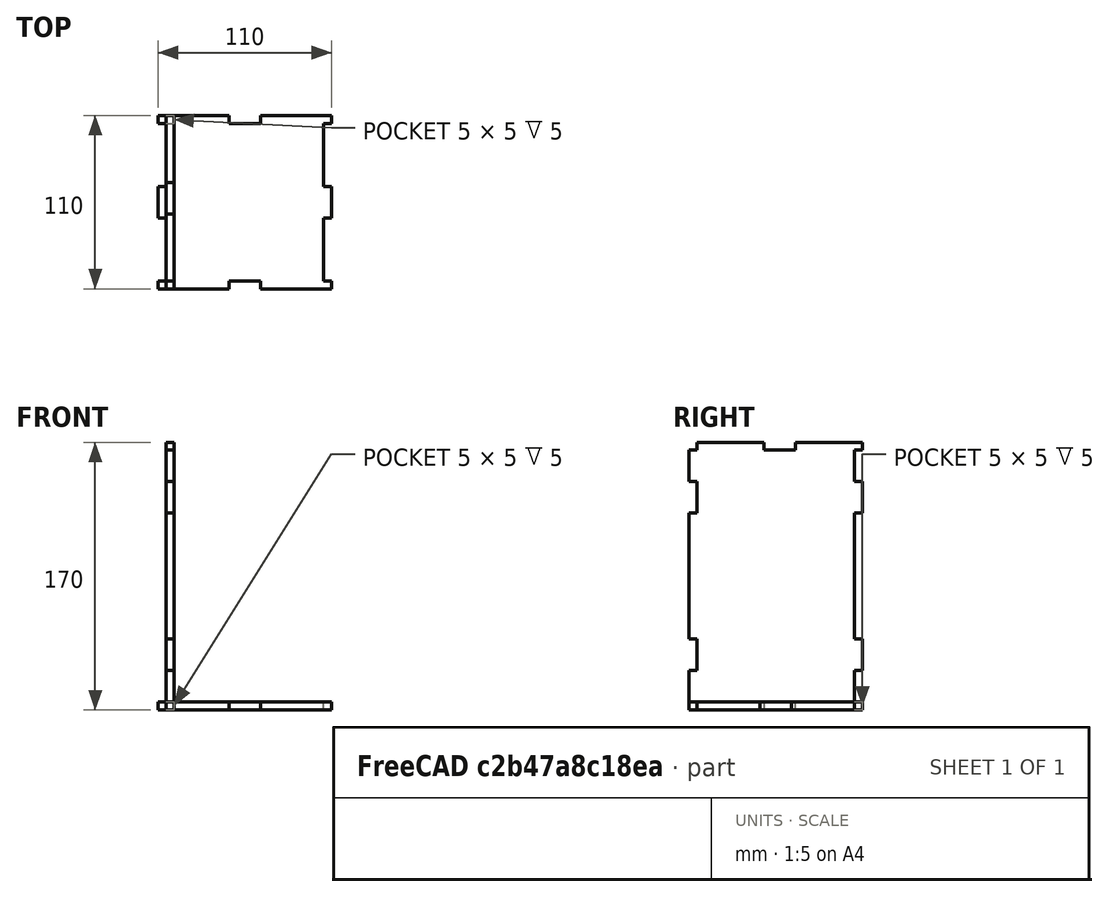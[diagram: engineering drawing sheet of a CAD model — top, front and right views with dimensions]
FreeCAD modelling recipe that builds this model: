
FCSTD DOCUMENT  (FreeCAD 0.19R)
Label: CAIXA-CLIENTE-04
License: Creative Commons Attribution-NonCommercial-ShareAlike
LicenseURL: http://creativecommons.org/licenses/by-nc-sa/4.0/
objects: Sketcher::SketchObject×2, Part::Extrusion×2, Spreadsheet::Sheet×1
note: 4 computed .brp shape members not serialized (recipe doc carries the construction recipe); baked Part::Feature solids carry a one-line shape summary decoded from their .brp

FEATURE [Spreadsheet::Sheet] Spreadsheet
  cells = A1=Espessura; B1(espessura)=5; A2=Altura; B2(altura)=170; A3=Largura; B3(largura)=110; A4=Comprimento; B4(comprimento)=110; A5=Conector; B5(conector)=20
FEATURE [Sketcher::SketchObject] Sketch001
  FullyConstrained = false
  expr: Constraints[157] = Spreadsheet.comprimento
  expr: Constraints[149] = Spreadsheet.conector
  expr: Constraints[147] = Spreadsheet.espessura
  expr: Constraints[142] = Spreadsheet.largura
  sketch-geometry (61):
    g0: LineSegment StartX=-5 StartY=0 StartZ=0 EndX=-5 EndY=5 EndZ=0
    g1: LineSegment StartX=-5 StartY=5 StartZ=0 EndX=0 EndY=5 EndZ=0
    g2: LineSegment StartX=0 StartY=5 StartZ=0 EndX=0 EndY=45 EndZ=0
    g3: LineSegment StartX=0 StartY=45 StartZ=0 EndX=-5 EndY=45 EndZ=0
    g4: LineSegment StartX=-5 StartY=45 StartZ=0 EndX=-5 EndY=65 EndZ=0
    g5: LineSegment StartX=-5 StartY=65 StartZ=0 EndX=0 EndY=65 EndZ=0
    g6: LineSegment StartX=0 StartY=65 StartZ=0 EndX=0 EndY=105 EndZ=0
    g7: LineSegment StartX=0 StartY=105 StartZ=0 EndX=-5 EndY=105 EndZ=0
    g8: LineSegment StartX=-5 StartY=105 StartZ=0 EndX=-5 EndY=110 EndZ=0
    g9: LineSegment StartX=-5 StartY=110 StartZ=0 EndX=40 EndY=110 EndZ=0
    g10: LineSegment StartX=40 StartY=110 StartZ=0 EndX=40 EndY=105 EndZ=0
    g11: LineSegment StartX=40 StartY=105 StartZ=0 EndX=60 EndY=105 EndZ=0
    g12: LineSegment StartX=60 StartY=105 StartZ=0 EndX=60 EndY=110 EndZ=0
    g13: LineSegment StartX=60 StartY=110 StartZ=0 EndX=105 EndY=110 EndZ=0
    g14: LineSegment StartX=105 StartY=110 StartZ=0 EndX=105 EndY=105 EndZ=0
    g15: LineSegment StartX=105 StartY=105 StartZ=0 EndX=100 EndY=105 EndZ=0
    g16: LineSegment StartX=100 StartY=105 StartZ=0 EndX=100 EndY=65 EndZ=0
    g17: LineSegment StartX=100 StartY=65 StartZ=0 EndX=105 EndY=65 EndZ=0
    g18: LineSegment StartX=105 StartY=65 StartZ=0 EndX=105 EndY=45 EndZ=0
    g19: LineSegment StartX=105 StartY=45 StartZ=0 EndX=100 EndY=45 EndZ=0
    g20: LineSegment StartX=100 StartY=45 StartZ=0 EndX=100 EndY=5 EndZ=0
    g21: LineSegment StartX=100 StartY=5 StartZ=0 EndX=105 EndY=5 EndZ=0
    g22: LineSegment StartX=105 StartY=5 StartZ=0 EndX=105 EndY=0 EndZ=0
    g23: LineSegment StartX=105 StartY=0 StartZ=0 EndX=60 EndY=0 EndZ=0
    g24: LineSegment StartX=60 StartY=0 StartZ=0 EndX=60 EndY=5 EndZ=0
    g25: LineSegment StartX=60 StartY=5 StartZ=0 EndX=40 EndY=5 EndZ=0
    g26: LineSegment StartX=40 StartY=5 StartZ=0 EndX=40 EndY=0 EndZ=0
    g27: LineSegment StartX=40 StartY=0 StartZ=0 EndX=-5 EndY=0 EndZ=0
    g28: LineSegment StartX=0 StartY=5 StartZ=0 EndX=0 EndY=0 EndZ=0
    g29: LineSegment StartX=0 StartY=0 StartZ=0 EndX=5 EndY=0 EndZ=0
    g30: LineSegment StartX=60 StartY=5 StartZ=0 EndX=105 EndY=5 EndZ=0
    g31: LineSegment StartX=40 StartY=0 StartZ=0 EndX=60 EndY=0 EndZ=0
    g32: LineSegment StartX=105 StartY=0 StartZ=0 EndX=100 EndY=0 EndZ=0
    g33: LineSegment StartX=100 StartY=0 StartZ=0 EndX=100 EndY=5 EndZ=0
    g34: LineSegment StartX=100 StartY=45 StartZ=0 EndX=100 EndY=65 EndZ=0
    g35: LineSegment StartX=100 StartY=105 StartZ=0 EndX=100 EndY=110 EndZ=0
    g36: LineSegment StartX=100 StartY=110 StartZ=0 EndX=105 EndY=110 EndZ=0
    g37: LineSegment StartX=60 StartY=110 StartZ=0 EndX=40 EndY=110 EndZ=0
    g38: LineSegment StartX=-5 StartY=110 StartZ=0 EndX=0 EndY=110 EndZ=0
    g39: LineSegment StartX=0 StartY=110 StartZ=0 EndX=0 EndY=105 EndZ=0
    g40: LineSegment StartX=0 StartY=65 StartZ=0 EndX=0 EndY=45 EndZ=0
    g41: LineSegment StartX=40 StartY=105 StartZ=0 EndX=-5 EndY=105 EndZ=0
    g42: LineSegment StartX=-5 StartY=105 StartZ=0 EndX=-5 EndY=65 EndZ=0
    g43: LineSegment StartX=-5 StartY=65 StartZ=0 EndX=40 EndY=65 EndZ=0
    g44: LineSegment StartX=40 StartY=65 StartZ=0 EndX=40 EndY=105 EndZ=0
    g45: LineSegment StartX=60 StartY=105 StartZ=0 EndX=105 EndY=105 EndZ=0
    g46: LineSegment StartX=105 StartY=105 StartZ=0 EndX=105 EndY=65 EndZ=0
    g47: LineSegment StartX=105 StartY=65 StartZ=0 EndX=60 EndY=65 EndZ=0
    g48: LineSegment StartX=60 StartY=65 StartZ=0 EndX=60 EndY=105 EndZ=0
    g49: LineSegment StartX=105 StartY=45 StartZ=0 EndX=60 EndY=45 EndZ=0
    g50: LineSegment StartX=60 StartY=45 StartZ=0 EndX=60 EndY=5 EndZ=0
    g51: LineSegment StartX=60 StartY=5 StartZ=0 EndX=105 EndY=5 EndZ=0
    g52: LineSegment StartX=105 StartY=5 StartZ=0 EndX=105 EndY=45 EndZ=0
    g53: LineSegment StartX=40 StartY=5 StartZ=0 EndX=-5 EndY=5 EndZ=0
    g54: LineSegment StartX=-5 StartY=5 StartZ=0 EndX=-5 EndY=45 EndZ=0
    g55: LineSegment StartX=-5 StartY=45 StartZ=0 EndX=40 EndY=45 EndZ=0
    g56: LineSegment StartX=40 StartY=45 StartZ=0 EndX=40 EndY=5 EndZ=0
    g57: LineSegment StartX=40 StartY=65 StartZ=0 EndX=60 EndY=65 EndZ=0
    g58: LineSegment StartX=60 StartY=65 StartZ=0 EndX=60 EndY=45 EndZ=0
    g59: LineSegment StartX=60 StartY=45 StartZ=0 EndX=40 EndY=45 EndZ=0
    g60: LineSegment StartX=40 StartY=45 StartZ=0 EndX=40 EndY=65 EndZ=0
  constraints (158):
    c: PointOnObject(g0,g-1)
    c: Vertical(g0)
    c: Coincident(g0,g1)
    c: PointOnObject(g1,g-2)
    c: Horizontal(g1)
    c: Coincident(g1,g2)
    c: PointOnObject(g2,g-2)
    c: Coincident(g2,g3)
    c: Horizontal(g3)
    c: Coincident(g3,g4)
    c: Vertical(g4)
    c: Coincident(g4,g5)
    c: PointOnObject(g5,g-2)
    c: Horizontal(g5)
    c: Coincident(g5,g6)
    c: PointOnObject(g6,g-2)
    c: Coincident(g6,g7)
    c: Horizontal(g7)
    c: Coincident(g7,g8)
    c: Vertical(g8)
    c: Coincident(g8,g9)
    c: Horizontal(g9)
    c: Coincident(g9,g10)
    c: Vertical(g10)
    c: Coincident(g10,g11)
    c: Horizontal(g11)
    c: Coincident(g11,g12)
    c: Vertical(g12)
    c: Coincident(g12,g13)
    c: Horizontal(g13)
    c: Coincident(g13,g14)
    c: Vertical(g14)
    c: Coincident(g14,g15)
    c: Horizontal(g15)
    c: Coincident(g15,g16)
    c: Vertical(g16)
    c: Coincident(g16,g17)
    c: Horizontal(g17)
    c: Coincident(g17,g18)
    c: Vertical(g18)
    c: Coincident(g18,g19)
    c: Horizontal(g19)
    c: Coincident(g19,g20)
    c: Vertical(g20)
    c: Coincident(g20,g21)
    c: Horizontal(g21)
    c: Coincident(g21,g22)
    c: PointOnObject(g22,g-1)
    c: Vertical(g22)
    c: Coincident(g22,g23)
    c: PointOnObject(g23,g-1)
    c: Coincident(g23,g24)
    c: Vertical(g24)
    c: Coincident(g24,g25)
    c: Horizontal(g25)
    c: Coincident(g25,g26)
    c: PointOnObject(g26,g-1)
    c: Vertical(g26)
    c: Coincident(g26,g27)
    c: Coincident(g27,g0)
    c: Coincident(g1,g28)
    c: PointOnObject(g28,g-1)
    c: Vertical(g28)
    c: Coincident(g28,g29)
    c: PointOnObject(g29,g27)
    c: Coincident(g24,g30)
    c: Coincident(g30,g21)
    c: Horizontal(g30)
    c: Coincident(g26,g31)
    c: Coincident(g31,g23)
    c: Coincident(g22,g32)
    c: PointOnObject(g32,g-1)
    c: Coincident(g32,g33)
    c: Coincident(g33,g20)
    c: Vertical(g33)
    c: Coincident(g19,g34)
    c: Coincident(g34,g16)
    c: Vertical(g34)
    c: Coincident(g15,g35)
    c: Vertical(g35)
    c: Coincident(g35,g36)
    c: Coincident(g36,g13)
    c: Horizontal(g36)
    c: Coincident(g12,g37)
    c: Coincident(g37,g9)
    c: Horizontal(g37)
    c: Coincident(g8,g38)
    c: PointOnObject(g38,g-2)
    c: Horizontal(g38)
    c: Coincident(g38,g39)
    c: Coincident(g39,g6)
    c: Coincident(g5,g40)
    c: Coincident(g40,g2)
    c: Coincident(g41,g42)
    c: Coincident(g42,g43)
    c: Coincident(g43,g44)
    c: Coincident(g44,g41)
    c: Horizontal(g41)
    c: Horizontal(g43)
    c: Vertical(g42)
    c: Vertical(g44)
    c: Coincident(g41,g10)
    c: Coincident(g42,g4)
    c: Coincident(g45,g46)
    c: Coincident(g46,g47)
    c: Coincident(g47,g48)
    c: Coincident(g48,g45)
    c: Horizontal(g45)
    c: Horizontal(g47)
    c: Vertical(g46)
    c: Vertical(g48)
    c: Coincident(g45,g11)
    c: Coincident(g46,g17)
    c: Coincident(g49,g50)
    c: Coincident(g50,g51)
    c: Coincident(g51,g52)
    c: Coincident(g52,g49)
    c: Horizontal(g49)
    c: Vertical(g50)
    c: Vertical(g52)
    c: Coincident(g49,g18)
    c: Coincident(g50,g24)
    c: Coincident(g53,g54)
    c: Coincident(g54,g55)
    c: Coincident(g55,g56)
    c: Coincident(g56,g53)
    c: Horizontal(g53)
    c: Horizontal(g55)
    c: Vertical(g54)
    c: Vertical(g56)
    c: Coincident(g53,g25)
    c: Coincident(g54,g3)
    c: Coincident(g57,g58)
    c: Coincident(g58,g59)
    c: Coincident(g59,g60)
    c: Coincident(g60,g57)
    c: Horizontal(g57)
    c: Horizontal(g59)
    c: Vertical(g58)
    c: Vertical(g60)
    c: Coincident(g57,g43)
    c: Coincident(g58,g49)
    c: DistanceY(g-1,g38) = 110
    c: Equal(g16,g20)
    c: Equal(g36,g35)
    c: Equal(g35,g38)
    c: Equal(g38,g33)
    c: DistanceY(g39,g39) = 5
    c: Equal(g37,g34)
    c: DistanceX(g37,g37) = 20
    c: Coincident(g14,g45)
    c: Coincident(g7,g41)
    c: Coincident(g47,g57)
    c: Coincident(g55,g59)
    c: Coincident(g0,g53)
    c: Coincident(g21,g51)
    c: Equal(g43,g47)
    c: DistanceX(g8,g13) = 110
FEATURE [Part::Extrusion] Extrude
  Base = -> Sketch001
  Dir = (0,0,1)
  DirMode = 2
  FaceMakerClass = Part::FaceMakerBullseye
  LengthFwd = 5
  LengthRev = 0
  Solid = true
  Symmetric = false
  expr: LengthFwd = Spreadsheet.espessura
FEATURE [Sketcher::SketchObject] Sketch
  FullyConstrained = true
  Placement = pos=(0,0,0) rot=(0.57735,0.57735,0.57735;2.0944rad)
  expr: Constraints[203] = Spreadsheet.largura
  expr: Constraints[151] = Spreadsheet.espessura
  expr: Constraints[125] = Spreadsheet.conector
  expr: Constraints[127] = Spreadsheet.altura
  sketch-geometry (82):
    g0: LineSegment StartX=0 StartY=0 StartZ=0 EndX=5 EndY=0 EndZ=0
    g1: LineSegment StartX=5 StartY=0 StartZ=0 EndX=5 EndY=5 EndZ=0
    g2: LineSegment StartX=5 StartY=5 StartZ=0 EndX=47.5 EndY=5 EndZ=0
    g3: LineSegment StartX=47.5 StartY=5 StartZ=0 EndX=47.5 EndY=0 EndZ=0
    g4: LineSegment StartX=47.5 StartY=0 StartZ=0 EndX=67.5 EndY=0 EndZ=0
    g5: LineSegment StartX=67.5 StartY=0 StartZ=0 EndX=67.5 EndY=5 EndZ=0
    g6: LineSegment StartX=67.5 StartY=5 StartZ=0 EndX=110 EndY=5 EndZ=0
    g7: LineSegment StartX=110 StartY=5 StartZ=0 EndX=110 EndY=0 EndZ=0
    g8: LineSegment StartX=110 StartY=0 StartZ=0 EndX=105 EndY=0 EndZ=0
    g9: LineSegment StartX=105 StartY=0 StartZ=0 EndX=105 EndY=25 EndZ=0
    g10: LineSegment StartX=105 StartY=125 StartZ=0 EndX=110 EndY=125 EndZ=0
    g11: LineSegment StartX=110 StartY=125 StartZ=0 EndX=110 EndY=145 EndZ=0
    g12: LineSegment StartX=110 StartY=145 StartZ=0 EndX=105 EndY=145 EndZ=0
    g13: LineSegment StartX=105 StartY=145 StartZ=0 EndX=105 EndY=165 EndZ=0
    g14: LineSegment StartX=105 StartY=165 StartZ=0 EndX=110 EndY=165 EndZ=0
    g15: LineSegment StartX=110 StartY=165 StartZ=0 EndX=110 EndY=170 EndZ=0
    g16: LineSegment StartX=110 StartY=170 StartZ=0 EndX=67.5 EndY=170 EndZ=0
    g17: LineSegment StartX=67.5 StartY=170 StartZ=0 EndX=67.5 EndY=165 EndZ=0
    g18: LineSegment StartX=67.5 StartY=165 StartZ=0 EndX=47.5 EndY=165 EndZ=0
    g19: LineSegment StartX=47.5 StartY=165 StartZ=0 EndX=47.5 EndY=170 EndZ=0
    g20: LineSegment StartX=47.5 StartY=170 StartZ=0 EndX=5 EndY=170 EndZ=0
    g21: LineSegment StartX=5 StartY=170 StartZ=0 EndX=5 EndY=165 EndZ=0
    g22: LineSegment StartX=5 StartY=165 StartZ=0 EndX=0 EndY=165 EndZ=0
    g23: LineSegment StartX=0 StartY=165 StartZ=0 EndX=0 EndY=145 EndZ=0
    g24: LineSegment StartX=0 StartY=145 StartZ=0 EndX=5 EndY=145 EndZ=0
    g25: LineSegment StartX=5 StartY=145 StartZ=0 EndX=5 EndY=125 EndZ=0
    g26: LineSegment StartX=5 StartY=125 StartZ=0 EndX=0 EndY=125 EndZ=0
    g27: LineSegment StartX=0 StartY=125 StartZ=0 EndX=0 EndY=145 EndZ=0
    g28: LineSegment StartX=0 StartY=125 StartZ=0 EndX=0 EndY=45 EndZ=0
    g29: LineSegment StartX=47.5 StartY=165 StartZ=0 EndX=5 EndY=165 EndZ=0
    g30: LineSegment StartX=5 StartY=165 StartZ=0 EndX=5 EndY=145 EndZ=0
    g31: LineSegment StartX=5 StartY=145 StartZ=0 EndX=47.5 EndY=145 EndZ=0
    g32: LineSegment StartX=47.5 StartY=145 StartZ=0 EndX=47.5 EndY=165 EndZ=0
    g33: LineSegment StartX=67.5 StartY=165 StartZ=0 EndX=110 EndY=165 EndZ=0
    g34: LineSegment StartX=110 StartY=165 StartZ=0 EndX=110 EndY=145 EndZ=0
    g35: LineSegment StartX=110 StartY=145 StartZ=0 EndX=67.5 EndY=145 EndZ=0
    g36: LineSegment StartX=67.5 StartY=145 StartZ=0 EndX=67.5 EndY=165 EndZ=0
    g37: LineSegment StartX=5 StartY=125 StartZ=0 EndX=47.5 EndY=125 EndZ=0
    g38: LineSegment StartX=47.5 StartY=125 StartZ=0 EndX=47.5 EndY=45 EndZ=0
    g39: LineSegment StartX=47.5 StartY=5 StartZ=0 EndX=5 EndY=5 EndZ=0
    g40: LineSegment StartX=5 StartY=5 StartZ=0 EndX=5 EndY=25 EndZ=0
    g41: LineSegment StartX=67.5 StartY=5 StartZ=0 EndX=110 EndY=5 EndZ=0
    g42: LineSegment StartX=110 StartY=5 StartZ=0 EndX=110 EndY=25 EndZ=0
    g43: LineSegment StartX=110 StartY=125 StartZ=0 EndX=67.5 EndY=125 EndZ=0
    g44: LineSegment StartX=67.5 StartY=125 StartZ=0 EndX=67.5 EndY=45 EndZ=0
    g45: LineSegment StartX=67.5 StartY=145 StartZ=0 EndX=47.5 EndY=145 EndZ=0
    g46: LineSegment StartX=47.5 StartY=145 StartZ=0 EndX=47.5 EndY=125 EndZ=0
    g47: LineSegment StartX=47.5 StartY=125 StartZ=0 EndX=67.5 EndY=125 EndZ=0
    g48: LineSegment StartX=67.5 StartY=125 StartZ=0 EndX=67.5 EndY=145 EndZ=0
    g49: LineSegment StartX=105 StartY=145 StartZ=0 EndX=105 EndY=125 EndZ=0
    g50: LineSegment StartX=47.5 StartY=5 StartZ=0 EndX=67.5 EndY=5 EndZ=0
    g51: LineSegment StartX=47.5 StartY=170 StartZ=0 EndX=67.5 EndY=170 EndZ=0
    g52: LineSegment StartX=5 StartY=170 StartZ=0 EndX=0 EndY=170 EndZ=0
    g53: LineSegment StartX=0 StartY=170 StartZ=0 EndX=0 EndY=165 EndZ=0
    g54: LineSegment StartX=105 StartY=165 StartZ=0 EndX=105 EndY=170 EndZ=0
    g55: LineSegment StartX=105 StartY=170 StartZ=0 EndX=110 EndY=170 EndZ=0
    g56: LineSegment StartX=5 StartY=5 StartZ=0 EndX=0 EndY=5 EndZ=0
    g57: LineSegment StartX=110 StartY=5 StartZ=0 EndX=105 EndY=5 EndZ=0
    g58: LineSegment StartX=67.5 StartY=0 StartZ=0 EndX=110 EndY=0 EndZ=0
    g59: LineSegment StartX=47.5 StartY=0 StartZ=0 EndX=5 EndY=0 EndZ=0
    g60: LineSegment StartX=0 StartY=25 StartZ=0 EndX=5 EndY=25 EndZ=0
    g61: LineSegment StartX=5 StartY=25 StartZ=0 EndX=47.5 EndY=25 EndZ=0
    g62: LineSegment StartX=47.5 StartY=25 StartZ=0 EndX=67.5 EndY=25 EndZ=0
    g63: LineSegment StartX=67.5 StartY=25 StartZ=0 EndX=110 EndY=25 EndZ=0
    g64: LineSegment StartX=110 StartY=25 StartZ=0 EndX=105 EndY=25 EndZ=0
    g65: LineSegment StartX=105 StartY=45 StartZ=0 EndX=110 EndY=45 EndZ=0
    g66: LineSegment StartX=110 StartY=45 StartZ=0 EndX=67.5 EndY=45 EndZ=0
    g67: LineSegment StartX=67.5 StartY=45 StartZ=0 EndX=47.5 EndY=45 EndZ=0
    g68: LineSegment StartX=47.5 StartY=45 StartZ=0 EndX=5 EndY=45 EndZ=0
    g69: LineSegment StartX=5 StartY=45 StartZ=0 EndX=0 EndY=45 EndZ=0
    g70: LineSegment StartX=0 StartY=25 StartZ=0 EndX=0 EndY=0 EndZ=0
    g71: LineSegment StartX=5 StartY=45 StartZ=0 EndX=5 EndY=125 EndZ=0
    g72: LineSegment StartX=47.5 StartY=25 StartZ=0 EndX=47.5 EndY=5 EndZ=0
    g73: LineSegment StartX=67.5 StartY=25 StartZ=0 EndX=67.5 EndY=5 EndZ=0
    g74: LineSegment StartX=110 StartY=45 StartZ=0 EndX=110 EndY=125 EndZ=0
    g75: LineSegment StartX=105 StartY=45 StartZ=0 EndX=105 EndY=125 EndZ=0
    g76: LineSegment StartX=105 StartY=45 StartZ=0 EndX=105 EndY=25 EndZ=0
    g77: LineSegment StartX=110 StartY=45 StartZ=0 EndX=110 EndY=25 EndZ=0
    g78: LineSegment StartX=67.5 StartY=45 StartZ=0 EndX=67.5 EndY=25 EndZ=0
    g79: LineSegment StartX=47.5 StartY=45 StartZ=0 EndX=47.5 EndY=25 EndZ=0
    g80: LineSegment StartX=5 StartY=45 StartZ=0 EndX=5 EndY=25 EndZ=0
    g81: LineSegment StartX=0 StartY=45 StartZ=0 EndX=0 EndY=25 EndZ=0
  constraints (205):
    c: PointOnObject(g0,g-1)
    c: Coincident(g0,g1)
    c: Vertical(g1)
    c: Coincident(g1,g2)
    c: Horizontal(g2)
    c: Coincident(g2,g3)
    c: Vertical(g3)
    c: Coincident(g3,g4)
    c: Horizontal(g4)
    c: Coincident(g4,g5)
    c: Vertical(g5)
    c: Coincident(g5,g6)
    c: Horizontal(g6)
    c: Coincident(g6,g7)
    c: Vertical(g7)
    c: Coincident(g7,g8)
    c: Horizontal(g8)
    c: Coincident(g8,g9)
    c: Vertical(g9)
    c: Coincident(g75,g10)
    c: Horizontal(g10)
    c: Coincident(g10,g11)
    c: Vertical(g11)
    c: Coincident(g11,g12)
    c: Horizontal(g12)
    c: Coincident(g12,g13)
    c: Vertical(g13)
    c: Coincident(g13,g14)
    c: Coincident(g14,g15)
    c: Vertical(g15)
    c: Coincident(g15,g16)
    c: Horizontal(g16)
    c: Coincident(g16,g17)
    c: Vertical(g17)
    c: Coincident(g17,g18)
    c: Coincident(g18,g19)
    c: Vertical(g19)
    c: Coincident(g19,g20)
    c: Horizontal(g20)
    c: Coincident(g21,g22)
    c: Horizontal(g22)
    c: Coincident(g25,g26)
    c: Horizontal(g24)
    c: Horizontal(g26)
    c: Coincident(g23,g24)
    c: Coincident(g28,g26)
    c: Coincident(g23,g27)
    c: Coincident(g26,g27)
    c: Horizontal(g18)
    c: Horizontal(g14)
    c: Coincident(g30,g31)
    c: Coincident(g31,g32)
    c: Coincident(g32,g29)
    c: Horizontal(g29)
    c: Horizontal(g31)
    c: Vertical(g32)
    c: Coincident(g29,g18)
    c: Coincident(g33,g34)
    c: Coincident(g34,g35)
    c: Coincident(g35,g36)
    c: Coincident(g36,g33)
    c: Horizontal(g33)
    c: Horizontal(g35)
    c: Vertical(g34)
    c: Vertical(g36)
    c: Coincident(g33,g17)
    c: Coincident(g34,g11)
    c: Coincident(g37,g38)
    c: Coincident(g72,g39)
    c: Coincident(g39,g40)
    c: Coincident(g71,g37)
    c: Horizontal(g37)
    c: Vertical(g38)
    c: Vertical(g40)
    c: Coincident(g37,g25)
    c: Coincident(g72,g2)
    c: Coincident(g41,g42)
    c: Coincident(g74,g43)
    c: Coincident(g43,g44)
    c: Coincident(g73,g41)
    c: Horizontal(g43)
    c: Vertical(g42)
    c: Vertical(g44)
    c: Coincident(g41,g5)
    c: Coincident(g74,g10)
    c: Coincident(g45,g46)
    c: Coincident(g46,g47)
    c: Coincident(g47,g48)
    c: Coincident(g48,g45)
    c: Horizontal(g45)
    c: Horizontal(g47)
    c: Vertical(g46)
    c: Vertical(g48)
    c: Coincident(g45,g35)
    c: Coincident(g46,g37)
    c: Coincident(g43,g47)
    c: Coincident(g31,g45)
    c: Coincident(g14,g33)
    c: Equal(g14,g15)
    c: Equal(g15,g22)
    c: Equal(g22,g7)
    c: Coincident(g6,g41)
    c: Coincident(g49,g12)
    c: Coincident(g49,g75)
    c: Vertical(g49)
    c: Coincident(g50,g2)
    c: Horizontal(g50)
    c: Coincident(g5,g50)
    c: Coincident(g51,g19)
    c: Coincident(g51,g16)
    c: Horizontal(g51)
    c: Coincident(g52,g53)
    c: Coincident(g53,g22)
    c: Horizontal(g52)
    c: Coincident(g13,g54)
    c: Coincident(g54,g55)
    c: Coincident(g55,g15)
    c: Horizontal(g55)
    c: Vertical(g54)
    c: Coincident(g1,g39)
    c: Coincident(g56,g1)
    c: Horizontal(g56)
    c: Coincident(g57,g6)
    c: PointOnObject(g57,g9)
    c: Horizontal(g57)
    c: DistanceX(g51,g51) = 20
    c: Equal(g11,g18)
    c: DistanceY(g0,g52) = 170
    c: Coincident(g58,g4)
    c: Coincident(g58,g7)
    c: Horizontal(g58)
    c: Vertical(g53)
    c: Vertical(g21)
    c: Coincident(g20,g21)
    c: Coincident(g20,g52)
    c: Coincident(g21,g29)
    c: Coincident(g21,g30)
    c: Coincident(g22,g23)
    c: Vertical(g23)
    c: Vertical(g30)
    c: Vertical(g28)
    c: Coincident(g24,g25)
    c: Coincident(g24,g30)
    c: Vertical(g25)
    c: Vertical(g27)
    c: Coincident(g0,g70)
    c: Coincident(g0,g-1)
    c: PointOnObject(g56,g28)
    c: Coincident(g59,g3)
    c: Horizontal(g59)
    c: Coincident(g0,g59)
    c: DistanceY(g54,g54) = 5
    c: Equal(g25,g23)
    c: Horizontal(g60)
    c: Coincident(g60,g61)
    c: Horizontal(g61)
    c: Coincident(g61,g62)
    c: Horizontal(g62)
    c: Coincident(g62,g63)
    c: Horizontal(g63)
    c: Coincident(g63,g64)
    c: Horizontal(g64)
    c: Horizontal(g65)
    c: Coincident(g65,g66)
    c: Horizontal(g66)
    c: Coincident(g66,g67)
    c: Horizontal(g67)
    c: Coincident(g67,g68)
    c: Horizontal(g68)
    c: Coincident(g68,g69)
    c: Horizontal(g69)
    c: Coincident(g28,g69)
    c: Coincident(g70,g60)
    c: Tangent(g28,g70)
    c: Coincident(g40,g60)
    c: Coincident(g71,g68)
    c: Tangent(g40,g71)
    c: Coincident(g38,g67)
    c: Coincident(g72,g61)
    c: Tangent(g38,g72)
    c: Coincident(g44,g66)
    c: Coincident(g73,g62)
    c: Tangent(g44,g73)
    c: Coincident(g42,g63)
    c: Coincident(g74,g65)
    c: Tangent(g42,g74)
    c: Coincident(g9,g64)
    c: Coincident(g75,g65)
    c: Tangent(g9,g75)
    c: Coincident(g76,g75)
    c: Coincident(g76,g9)
    c: Coincident(g77,g65)
    c: Coincident(g77,g42)
    c: Coincident(g78,g44)
    c: Coincident(g78,g62)
    c: Coincident(g79,g38)
    c: Coincident(g79,g61)
    c: Coincident(g80,g68)
    c: Coincident(g80,g40)
    c: Coincident(g81,g28)
    c: Coincident(g81,g70)
    c: Equal(g72,g79)
    c: Equal(g79,g25)
    c: DistanceX(g52,g15) = 110
    c: Equal(g29,g33)
FEATURE [Part::Extrusion] Extrude001
  Base = -> Sketch
  Dir = (1,0,0)
  DirMode = 2
  FaceMakerClass = Part::FaceMakerBullseye
  LengthFwd = 5
  LengthRev = 0
  Solid = true
  Symmetric = false
  expr: LengthFwd = Spreadsheet.espessura
